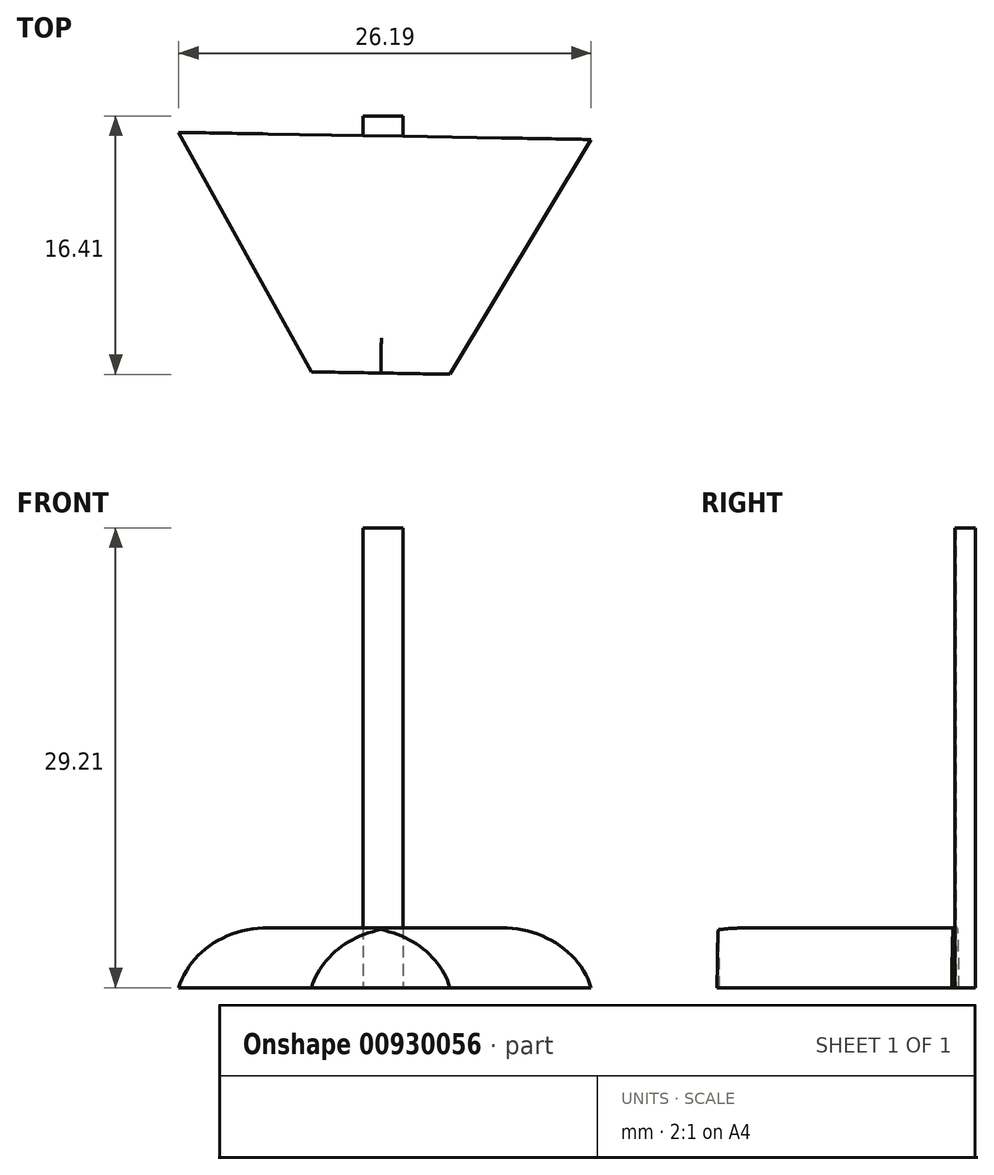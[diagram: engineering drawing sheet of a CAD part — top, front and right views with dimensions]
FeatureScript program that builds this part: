
annotation { "Feature Type Name" : "Feature", "Feature Type Description" : "" }
export const myFeature = defineFeature(function(context is Context, id is Id, definition is map)
    precondition{}
    {
        {
            var Q0;
            Q0=qCreatedBy(makeId("Top.planeOp"),FACE);
            var sketch = newSketch(context, id + "F0", { "sketchPlane" : qUnion([Q0])});
            skCircle(sketch, "E0.cCircle", {"center": v(0, 0) * mm, "radius": 15.12 * mm, "construction": true});
            skLineSegment(sketch, "E0.0", {"start": v(13.23, 7.33) * mm, "end": v(-0.26, -15.12) * mm});
            skLineSegment(sketch, "E0.1", {"start": v(-0.26, -15.12) * mm, "end": v(-12.96, 7.79) * mm});
            skLineSegment(sketch, "E0.2", {"start": v(-12.96, 7.79) * mm, "end": v(13.23, 7.33) * mm});
            skSolve(sketch);
        }
        {
            var Q0;
            Q0=makeQuery(id+"F0.imprint","IMPRINT",FACE,{"disambiguationData":[TD([[makeQuery(id+"F0.imprint","IMPRINT",EDGE,{"derivedFrom":sQuery(id+"F0.wireOp",EDGE,"E0.0")}),-1.0]])]});
            extrude(context, id + "F1", {"entities" : qUnion([Q0]), "depth" : 3.8 * mm, "offsetDistance" : 25.4 * mm});
        }
        {
            var Q0;
            Q0=makeQuery(id+"F1.opExtrude","SWEPT_EDGE",EDGE,{"disambiguationData":[OSD([sQuery(id+"F0.wireOp",EDGE,"E0.0"),sQuery(id+"F0.wireOp",EDGE,"E0.1")])]});
            chamfer(context, id + "F2", {"entities" : qUnion([Q0]), "width" : 5.08 * mm, "tangentPropagation" : true});
        }
        {
            var Q0;
            Q0=makeQuery(id+"F1.opExtrude","CAP_EDGE",EDGE,{"disambiguationData":[OSD([sQuery(id+"F0.wireOp",EDGE,"E0.0")])],"isStart":false});
            var Q1;
            Q1=makeQuery(id+"F1.opExtrude","CAP_EDGE",EDGE,{"disambiguationData":[OSD([sQuery(id+"F0.wireOp",EDGE,"E0.1")])],"isStart":false});
            fillet(context, id + "F3", {"entities" : qUnion([Q0, Q1]), "radius" : 5.08 * mm, "tangentPropagation" : true, "allowEdgeOverflow" : false});
        }
        {
            var Q0;
            Q0=makeQuery(id+"F1.opExtrude","CAP_FACE",FACE,{"disambiguationData":[OSD([sQuery(id+"F0.wireOp",EDGE,"E0.0"),sQuery(id+"F0.wireOp",EDGE,"E0.1"),sQuery(id+"F0.wireOp",EDGE,"E0.2")])],"isStart":false});
            var sketch = newSketch(context, id + "F4", { "sketchPlane" : qUnion([Q0])});
            skLineSegment(sketch, "E1.bottom", {"start": v(1.27, 8.83) * mm, "end": v(-1.27, 8.83) * mm});
            skLineSegment(sketch, "E1.top", {"start": v(1.27, 6.3) * mm, "end": v(-1.27, 6.3) * mm});
            skLineSegment(sketch, "E1.left", {"start": v(1.27, 8.83) * mm, "end": v(1.27, 6.3) * mm});
            skLineSegment(sketch, "E1.right", {"start": v(-1.27, 8.83) * mm, "end": v(-1.27, 6.3) * mm});
            skPoint(sketch, "E1.middle", {"position": v(0, 7.56) * mm});
            skSolve(sketch);
        }
        {
            var Q0;
            {var subQ0=sQuery(id+"F4.wireOp",EDGE,"E1.bottom");Q0=makeQuery(id+"F4.imprint","IMPRINT",FACE,{"disambiguationData":[TD([[makeQuery(id+"F4.imprint","IMPRINT",EDGE,{"derivedFrom":subQ0}),1.0]])]});}
            extrude(context, id + "F5", {"entities" : qUnion([Q0]), "operationType" : NewBodyOperationType.ADD, "depth" : 25.4 * mm, "offsetDistance" : 25.4 * mm, "hasSecondDirection" : true, "secondDirectionOppositeDirection" : true, "secondDirectionDepth" : 3.8 * mm});
        }
    });
